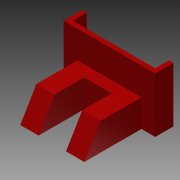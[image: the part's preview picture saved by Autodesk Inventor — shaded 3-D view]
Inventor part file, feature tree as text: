
AUTODESK INVENTOR PART (.ipt)
format: ipt  version: 2013 (Build 170138000, 138)  size: 127,488 bytes
history: native  units: mm
features: extrude x5, sketch x5, other x1
ambient origin geometry x8: Origin, YZ Plane, XZ Plane, XY Plane, X Axis, Y Axis, Z Axis, Center Point
feature tree (11):
  other  "ソリッド1"
  extrude  "押し出し1"  Depth=30.0mm
  extrude  "押し出し4"  Depth=70.0mm TaperAngle=0.0deg
  extrude  "押し出し5"  Depth=67.395mm
  extrude  "押し出し6"  Depth=49.705mm
  extrude  "押し出し7"  Depth=50.0mm
  sketch  "スケッチ1"
  sketch  "スケッチ7"
  sketch  "スケッチ8"
  sketch  "スケッチ9"
  sketch  "スケッチ10"
